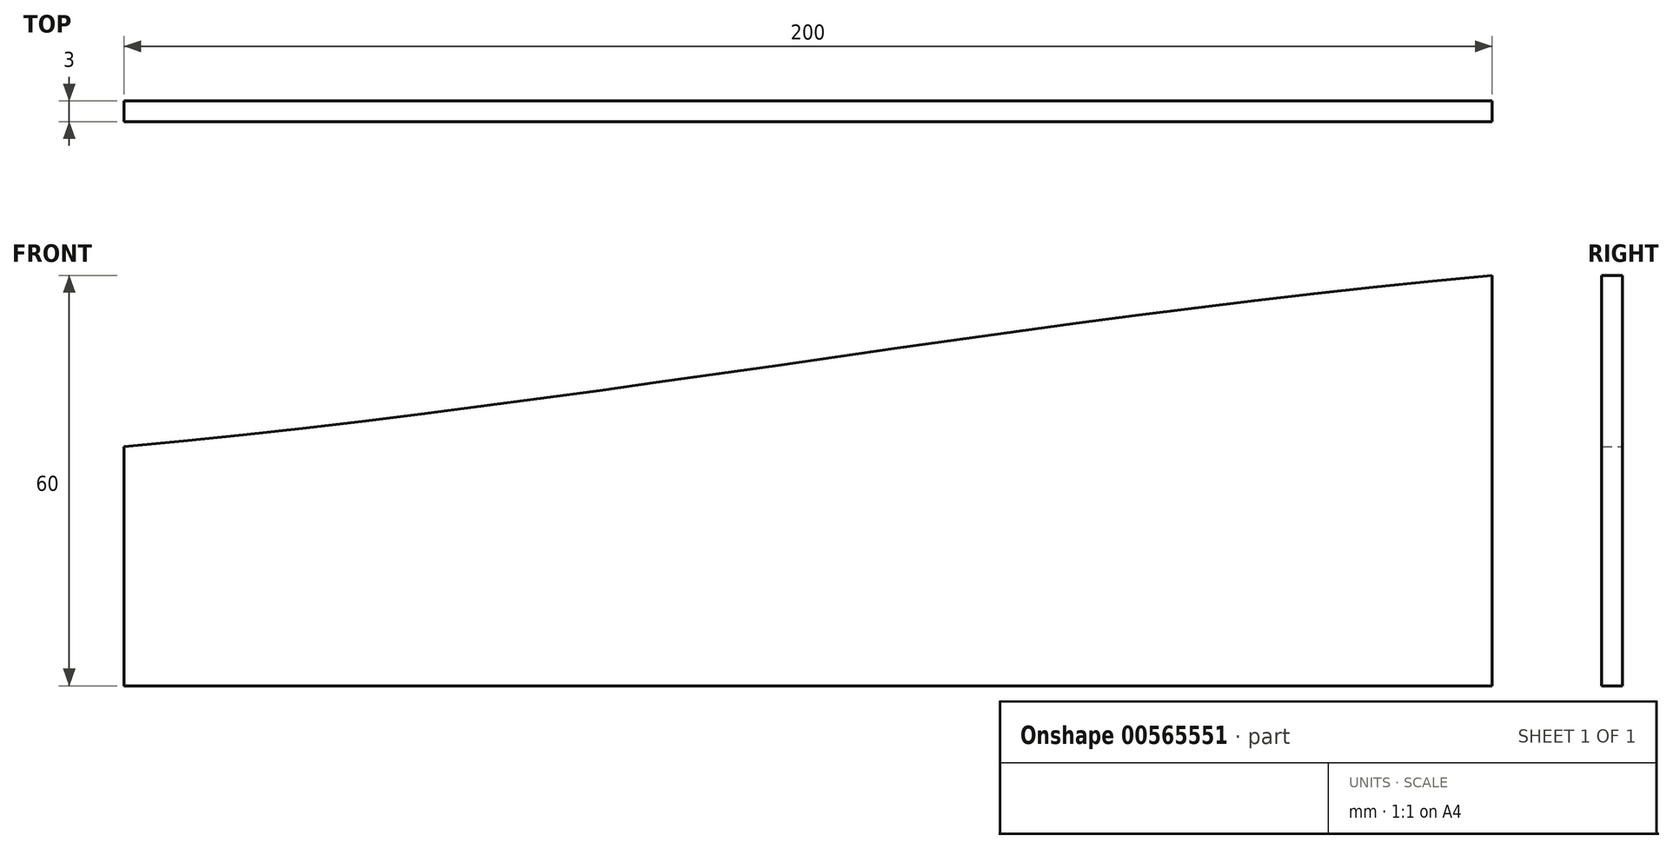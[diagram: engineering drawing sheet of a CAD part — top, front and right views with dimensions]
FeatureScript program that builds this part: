
annotation { "Feature Type Name" : "Feature", "Feature Type Description" : "" }
export const myFeature = defineFeature(function(context is Context, id is Id, definition is map)
    precondition{}
    {
        {
            var Q0;
            Q0=qCreatedBy(makeId("Front.planeOp"),FACE);
            var sketch = newSketch(context, id + "F0", { "sketchPlane" : qUnion([Q0])});
            skLineSegment(sketch, "E0.bottom", {"start": v(100, -30) * mm, "end": v(-100, -30) * mm});
            skLineSegment(sketch, "E0.top", {"start": v(100, 30) * mm, "end": v(-100, 30) * mm});
            skLineSegment(sketch, "E0.left", {"start": v(100, -30) * mm, "end": v(100, 30) * mm});
            skLineSegment(sketch, "E0.right", {"start": v(-100, -30) * mm, "end": v(-100, 30) * mm});
            skPoint(sketch, "E0.middle", {"position": v(0, 0) * mm});
            skFitSpline(sketch, "E1", {"points": [v(-100, 5) * mm, v(100, 30) * mm], "startDerivative": vector(200, 17.76) * mm, "endDerivative": vector(200, 17.76) * mm});
            skSolve(sketch);
        }
        {
            var Q0;
            {var subQ0=sQuery(id+"F0.wireOp",EDGE,"E0.bottom");Q0=makeQuery(id+"F0.imprint","IMPRINT",FACE,{"disambiguationData":[TD([[makeQuery(id+"F0.imprint","IMPRINT",EDGE,{"derivedFrom":subQ0}),-1.0]])]});}
            extrude(context, id + "F1", {"entities" : qUnion([Q0]), "depth" : 3 * mm, "offsetDistance" : 25 * mm});
        }
    });
